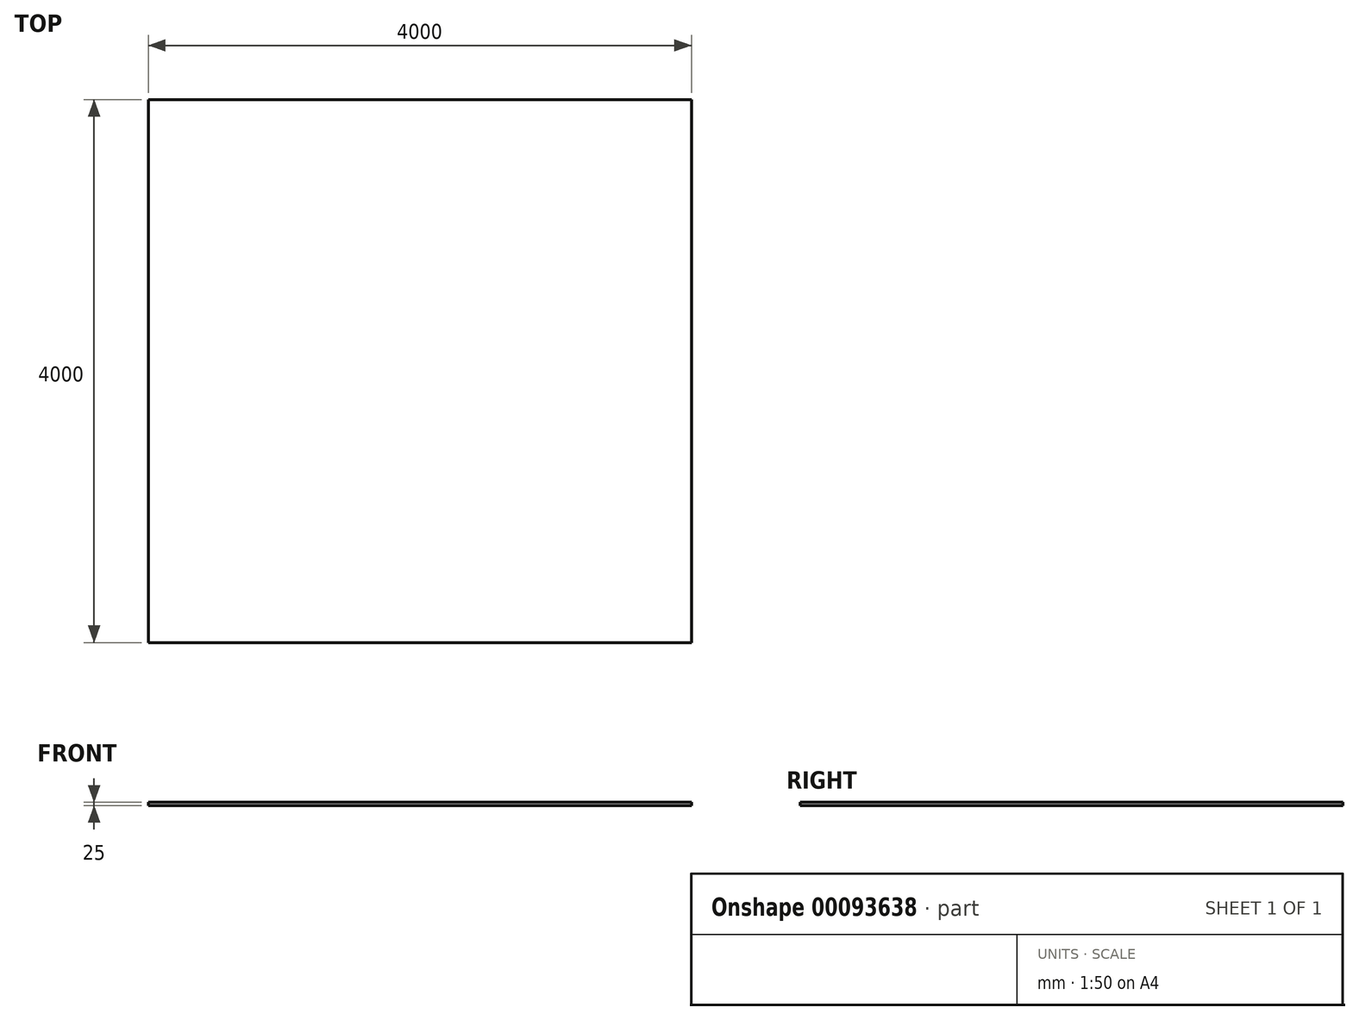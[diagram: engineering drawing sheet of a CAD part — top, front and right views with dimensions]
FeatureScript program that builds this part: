
annotation { "Feature Type Name" : "Feature", "Feature Type Description" : "" }
export const myFeature = defineFeature(function(context is Context, id is Id, definition is map)
    precondition{}
    {
        {
            var Q0;
            Q0=qCreatedBy(makeId("Top.planeOp"),FACE);
            var sketch = newSketch(context, id + "F0", { "sketchPlane" : qUnion([Q0])});
            skLineSegment(sketch, "E0.bottom", {"start": v(-2000, -2000) * mm, "end": v(2000, -2000) * mm});
            skLineSegment(sketch, "E0.top", {"start": v(-2000, 2000) * mm, "end": v(2000, 2000) * mm});
            skLineSegment(sketch, "E0.left", {"start": v(-2000, -2000) * mm, "end": v(-2000, 2000) * mm});
            skLineSegment(sketch, "E0.right", {"start": v(2000, -2000) * mm, "end": v(2000, 2000) * mm});
            skPoint(sketch, "E0.middle", {"position": v(0, 0) * mm});
            skSolve(sketch);
        }
        {
            var Q0;
            Q0 = qSketchRegion(id + "F0", true);
            extrude(context, id + "F1", {"entities" : qUnion([Q0]), "depth" : 25 * mm});
        }
    });
